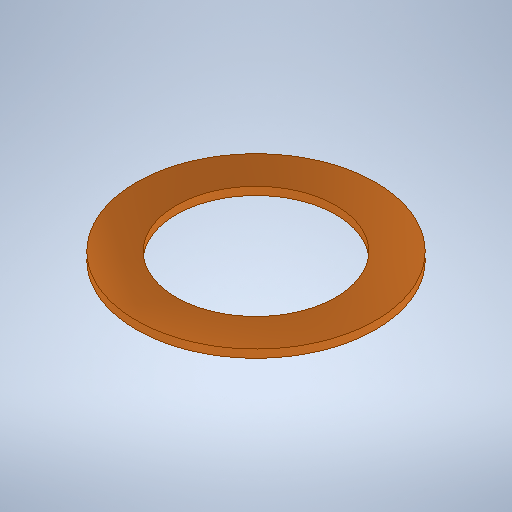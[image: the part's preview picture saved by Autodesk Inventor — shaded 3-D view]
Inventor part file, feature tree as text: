
AUTODESK INVENTOR PART (.ipt)
format: ipt  version: 2025.1 (Build 291241000, 241)  size: 246,272 bytes
history: native  units: mm
features: extrude x1, sketch x1
ambient origin geometry x8: Origin, YZ Plane, XZ Plane, XY Plane, X Axis, Y Axis, Z Axis, Center Point
bodies: Solid1 (feature_tree)
feature tree (2):
  extrude  "Extrusion1"  Depth=1.0mm
  sketch  "Sketch1"  dims[d0=30.0mm d1=20.0mm d2=1.0mm d3=0.0mm]
